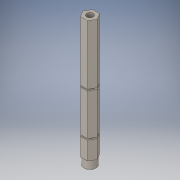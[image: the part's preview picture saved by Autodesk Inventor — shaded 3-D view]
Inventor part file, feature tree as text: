
AUTODESK INVENTOR PART (.ipt)
format: ipt  version: 2018 (Build 220112000, 112)  size: 132,608 bytes
history: native  units: in
note: dims shown in document units (in); Inventor stores cm internally (conversion verified against a paired STEP export)
features: chamfer x1
ambient origin geometry x8: Origin, YZ Plane, XZ Plane, XY Plane, X Axis, Y Axis, Z Axis, Center Point
bodies: Solid1 (feature_tree)
feature tree (1):
  chamfer  "Chamfer1"  [1 undecoded]
note: 1 required parameter value undecoded (feature->parameter linkage not recoverable at this tier; creation-order binding heuristic only, values carry confidence <= 0.55)
